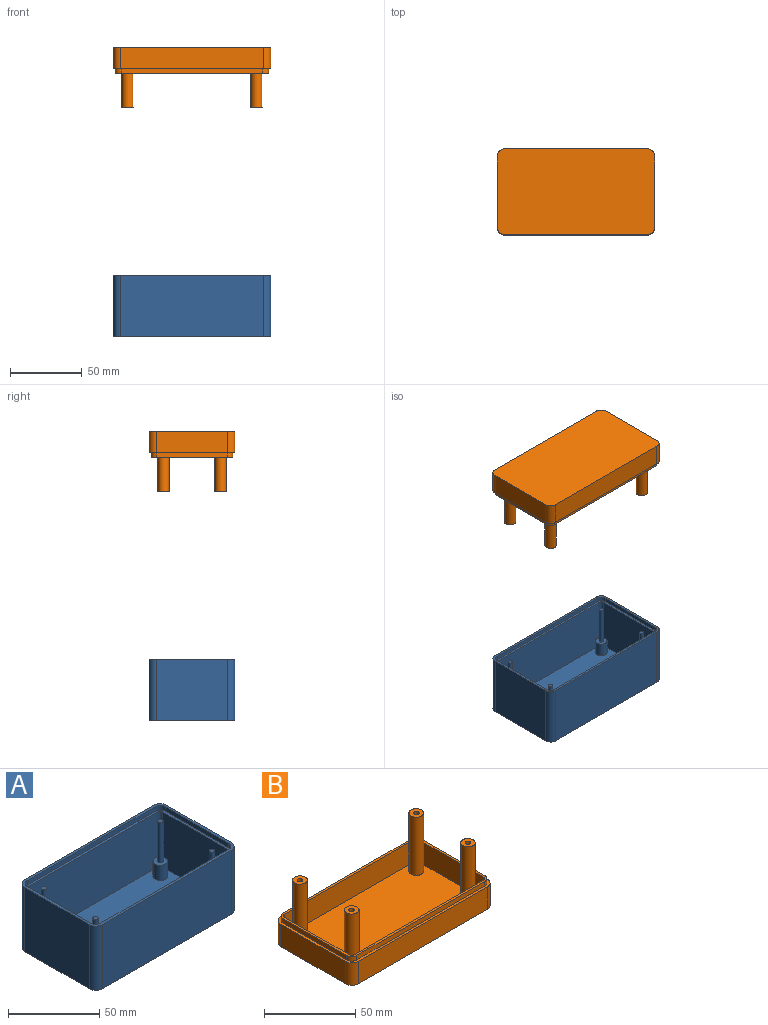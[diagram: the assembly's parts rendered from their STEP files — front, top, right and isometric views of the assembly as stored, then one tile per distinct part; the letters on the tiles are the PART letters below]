
ASSEMBLY  parts=2 mates=1
PART A: 60 faces, bbox 110x60x43 mm
  f0: plane 104x54mm, normal (0,0,1), area 5051.5mm2, adj f3,f4,f5,f6,f7,f8,f9,f10
  f1: plane 110x60mm, normal (0,0,-1), area 6218.5mm2, adj f20,f21,f22,f23,f24,f25,f26,f27
  f2: plane 107x57mm, normal (0,0,1), area 472.7mm2, adj f3,f4,f5,f6,f7,f8,f9,f10
  f3: plane 50x37mm, normal (-1,0,0), area 1850mm2, adj f0,f2,f4,f10
  f4: cylinder r=2mm len=37mm, axis (0,0,-1), area 116.2mm2, adj f0,f2,f3,f5
  f5: plane 100x37mm, normal (0,-1,0), area 3700mm2, adj f0,f2,f4,f6
  f6: cylinder r=2mm len=37mm, axis (0,0,-1), area 116.2mm2, adj f0,f2,f5,f7
  f7: plane 50x37mm, normal (1,0,0), area 1850mm2, adj f0,f2,f6,f8
  f8: cylinder r=2mm len=37mm, axis (0,0,-1), area 116.2mm2, adj f0,f2,f7,f9
  f9: plane 100x37mm, normal (0,1,0), area 3700mm2, adj f0,f2,f8,f10
  f10: cylinder r=2mm len=37mm, axis (0,0,-1), area 116.2mm2, adj f0,f2,f3,f9
  f11: cylinder r=4mm len=4mm, axis (0,0,-1), area 18.8mm2, adj f2,f12,f18,f19
  f12: plane 49x3mm, normal (-1,0,0), area 147mm2, adj f2,f11,f13,f19
  f13: cylinder r=4mm len=4mm, axis (0,0,-1), area 18.8mm2, adj f2,f12,f14,f19
  f14: plane 99x3mm, normal (0,1,0), area 297mm2, adj f2,f13,f15,f19
  f15: cylinder r=4mm len=4mm, axis (0,0,-1), area 18.8mm2, adj f2,f14,f16,f19
  f16: plane 49x3mm, normal (1,0,0), area 147mm2, adj f2,f15,f17,f19
  f17: cylinder r=4mm len=4mm, axis (0,0,-1), area 18.8mm2, adj f2,f16,f18,f19
  f18: plane 99x3mm, normal (0,-1,0), area 297mm2, adj f2,f11,f17,f19
  f19: plane 110x60mm, normal (0,0,1), area 493.3mm2, adj f11,f12,f13,f14,f15,f16,f17,f18
  f20: cylinder r=5mm len=43mm, axis (0,0,-1), area 337.7mm2, adj f1,f19,f21,f27
  f21: plane 100x43mm, normal (0,-1,0), area 4300mm2, adj f1,f19,f20,f22
  f22: cylinder r=5mm len=43mm, axis (0,0,-1), area 337.7mm2, adj f1,f19,f21,f23
  f23: plane 50x43mm, normal (-1,0,0), area 2150mm2, adj f1,f19,f22,f24
  f24: cylinder r=5mm len=43mm, axis (0,0,-1), area 337.7mm2, adj f1,f19,f23,f25
  f25: plane 100x43mm, normal (0,1,0), area 4300mm2, adj f1,f19,f24,f26
  f26: cylinder r=5mm len=43mm, axis (0,0,-1), area 337.7mm2, adj f1,f19,f25,f27
  f27: plane 50x43mm, normal (1,0,0), area 2150mm2, adj f1,f19,f20,f26
  f28: cylinder r=4mm len=10mm, axis (0,0,-1), area 251.3mm2, adj f0,f29
  f29: plane 8x8mm, normal (0,0,1), area 43.2mm2, adj f28,f36
  f30: cylinder r=4mm len=10mm, axis (0,0,-1), area 251.3mm2, adj f0,f31
  f31: plane 8x8mm, normal (0,0,1), area 43.2mm2, adj f30,f38
  f32: cylinder r=4mm len=10mm, axis (0,0,-1), area 251.3mm2, adj f0,f33
  f33: plane 8x8mm, normal (0,0,1), area 43.2mm2, adj f32,f40
  f34: cylinder r=4mm len=10mm, axis (0,0,-1), area 251.3mm2, adj f0,f35
  f35: plane 8x8mm, normal (0,0,1), area 43.2mm2, adj f34,f42
  f36: cylinder r=1.5mm len=27mm, axis (0,0,-1), area 254.5mm2, adj f29,f37
  f37: plane 3x3mm, normal (0,0,1), area 7.1mm2, adj f36
  f38: cylinder r=1.5mm len=27mm, axis (0,0,-1), area 254.5mm2, adj f31,f39
  f39: plane 3x3mm, normal (0,0,1), area 7.1mm2, adj f38
  f40: cylinder r=1.5mm len=27mm, axis (0,0,-1), area 254.5mm2, adj f33,f41
  f41: plane 3x3mm, normal (0,0,1), area 7.1mm2, adj f40
  f42: cylinder r=1.5mm len=27mm, axis (0,0,-1), area 254.5mm2, adj f35,f43
  f43: plane 3x3mm, normal (0,0,1), area 7.1mm2, adj f42
  f44: plane 3x3mm, normal (0,1,0), area 9mm2, adj f0,f1,f45,f47
  f45: plane 30x3mm, normal (1,0,0), area 90mm2, adj f0,f1,f44,f46
  f46: plane 3x3mm, normal (0,-1,0), area 9mm2, adj f0,f1,f45,f47
  f47: plane 30x3mm, normal (-1,0,0), area 90mm2, adj f0,f1,f44,f46
  f48: plane 3x3mm, normal (0,1,0), area 9mm2, adj f0,f1,f49,f51
  f49: plane 30x3mm, normal (1,0,0), area 90mm2, adj f0,f1,f48,f50
  f50: plane 3x3mm, normal (0,-1,0), area 9mm2, adj f0,f1,f49,f51
  f51: plane 30x3mm, normal (-1,0,0), area 90mm2, adj f0,f1,f48,f50
  f52: plane 3x3mm, normal (0,1,0), area 9mm2, adj f0,f1,f53,f55
  f53: plane 30x3mm, normal (1,0,0), area 90mm2, adj f0,f1,f52,f54
  f54: plane 3x3mm, normal (0,-1,0), area 9mm2, adj f0,f1,f53,f55
  f55: plane 30x3mm, normal (-1,0,0), area 90mm2, adj f0,f1,f52,f54
  f56: plane 3x3mm, normal (0,1,0), area 9mm2, adj f0,f1,f57,f59
  f57: plane 30x3mm, normal (1,0,0), area 90mm2, adj f0,f1,f56,f58
  f58: plane 3x3mm, normal (0,-1,0), area 9mm2, adj f0,f1,f57,f59
  f59: plane 30x3mm, normal (-1,0,0), area 90mm2, adj f0,f1,f56,f58
PART B: 44 faces, bbox 110x60x42 mm
  f0: plane 107x57mm, normal (0,0,1), area 472.7mm2, adj f1,f2,f3,f4,f5,f6,f7,f8
  f1: plane 50x15mm, normal (-1,0,0), area 750mm2, adj f0,f2,f8,f9
  f2: cylinder r=2mm len=15mm, axis (0,0,-1), area 47.1mm2, adj f0,f1,f3,f9
  f3: plane 100x15mm, normal (0,-1,0), area 1500mm2, adj f0,f2,f4,f9
  f4: cylinder r=2mm len=15mm, axis (0,0,-1), area 47.1mm2, adj f0,f3,f5,f9
  f5: plane 50x15mm, normal (1,0,0), area 750mm2, adj f0,f4,f6,f9
  f6: cylinder r=2mm len=15mm, axis (0,0,-1), area 47.1mm2, adj f0,f5,f7,f9
  f7: plane 100x15mm, normal (0,1,0), area 1500mm2, adj f0,f6,f8,f9
  f8: cylinder r=2mm len=15mm, axis (0,0,-1), area 47.1mm2, adj f0,f1,f7,f9
  f9: plane 104x54mm, normal (0,0,1), area 5411.5mm2, adj f1,f2,f3,f4,f5,f6,f7,f8
  f10: cylinder r=4mm len=4mm, axis (0,0,1), area 18.8mm2, adj f0,f11,f17,f18
  f11: plane 49x3mm, normal (1,0,0), area 147mm2, adj f0,f10,f12,f18
  f12: cylinder r=4mm len=4mm, axis (0,0,1), area 18.8mm2, adj f0,f11,f13,f18
  f13: plane 99x3mm, normal (0,-1,0), area 297mm2, adj f0,f12,f14,f18
  f14: cylinder r=4mm len=4mm, axis (0,0,1), area 18.8mm2, adj f0,f13,f15,f18
  f15: plane 49x3mm, normal (-1,0,0), area 147mm2, adj f0,f14,f16,f18
  f16: cylinder r=4mm len=4mm, axis (0,0,1), area 18.8mm2, adj f0,f15,f17,f18
  f17: plane 99x3mm, normal (0,1,0), area 297mm2, adj f0,f10,f16,f18
  f18: plane 110x60mm, normal (0,0,1), area 493.3mm2, adj f10,f11,f12,f13,f14,f15,f16,f17
  f19: plane 110x60mm, normal (0,0,-1), area 6578.5mm2, adj f20,f21,f22,f23,f24,f25,f26,f27
  f20: cylinder r=5mm len=15mm, axis (0,0,-1), area 117.8mm2, adj f18,f19,f21,f27
  f21: plane 100x15mm, normal (0,-1,0), area 1500mm2, adj f18,f19,f20,f22
  f22: cylinder r=5mm len=15mm, axis (0,0,-1), area 117.8mm2, adj f18,f19,f21,f23
  f23: plane 50x15mm, normal (-1,0,0), area 750mm2, adj f18,f19,f22,f24
  f24: cylinder r=5mm len=15mm, axis (0,0,-1), area 117.8mm2, adj f18,f19,f23,f25
  f25: plane 100x15mm, normal (0,1,0), area 1500mm2, adj f18,f19,f24,f26
  f26: cylinder r=5mm len=15mm, axis (0,0,-1), area 117.8mm2, adj f18,f19,f25,f27
  f27: plane 50x15mm, normal (1,0,0), area 750mm2, adj f18,f19,f20,f26
  f28: cylinder r=4mm len=39mm, axis (0,0,-1), area 980.2mm2, adj f9,f29
  f29: plane 8x8mm, normal (0,0,1), area 43.2mm2, adj f28,f42
  f30: cylinder r=4mm len=39mm, axis (0,0,-1), area 980.2mm2, adj f9,f31
  f31: plane 8x8mm, normal (0,0,1), area 43.2mm2, adj f30,f40
  f32: cylinder r=4mm len=39mm, axis (0,0,-1), area 980.2mm2, adj f9,f33
  f33: plane 8x8mm, normal (0,0,1), area 43.2mm2, adj f32,f38
  f34: cylinder r=4mm len=39mm, axis (0,0,-1), area 980.2mm2, adj f9,f35
  f35: plane 8x8mm, normal (0,0,1), area 43.2mm2, adj f34,f36
  f36: cylinder r=1.5mm len=27mm, axis (0,0,1), area 254.5mm2, adj f35,f37
  f37: plane 3x3mm, normal (0,0,1), area 7.1mm2, adj f36
  f38: cylinder r=1.5mm len=27mm, axis (0,0,1), area 254.5mm2, adj f33,f39
  f39: plane 3x3mm, normal (0,0,1), area 7.1mm2, adj f38
  f40: cylinder r=1.5mm len=27mm, axis (0,0,1), area 254.5mm2, adj f31,f41
  f41: plane 3x3mm, normal (0,0,1), area 7.1mm2, adj f40
  f42: cylinder r=1.5mm len=27mm, axis (0,0,1), area 254.5mm2, adj f29,f43
  f43: plane 3x3mm, normal (0,0,1), area 7.1mm2, adj f42
PLACE A t=(-6.21,10.75,-7.18)mm fixed
PLACE B rot(axis=(0,1,0),180deg) t=(42.22,10.75,194.77)mm
MATE slider A.f28 <-> B.f30  axis (0,0,-1) through (-26.99,38.61,32.82)mm
